# Revit family: LAMP_FIL 35 CORNER OPAL COMFORT TRIMLESS HC
name_source: partatom
category: Luminarias
revit_build: Autodesk Revit 2018 (Build: 20190510_1515(x64)
units: mm (PartAtom-declared; Revit-internal decimal feet)

## family parameters
Anfitrión = Cara
Compartido = No
Corte con vacíos al cargar = No
Cota de conector redondo = Diámetro de uso
Origen de luz = Sí
Punto de cálculo de habitación = No
Tipo de pieza = Normal

## types (4) — shared parameters
Archivo de red fotométrica = F31SF084LOOP830NB.IES
CRI = 80
Cambio de temperatura de color de luz atenuada = <Ninguno>
Dimensions = 311x311x35
Elevación por defecto = 1219 mm
Fabricante = LAMP
Filtro de color = 16777215
Finish = Matte white RAL 9010
Gear = Electronic
IEE = A+
Installation instructions = https://www.lamp.es
Insulation class = I
LED Lifetime = 60.000 L80 B10
Lamp = MID-POWER LED
Last update = 24/05/2021
MacAdam = 3
Manufacturer URL = http://www.lamp.es
Manufacturer country = Spain
Manufacturer name = LAMP
Material difusor = LAMP_PC Difusor Opal Fil
Material suspension = LAMP_Acero genérico
Plum = 6 W
Power = 5 W
Power Supply = 220-240V 50/60Hz
Product URL = https://www.lamp.es
Product datasheet = http://www.lamp.es
Protection rating = IP20 / IK07
Recessed dimensions = 317x317x52
Type = MID POWER TRIDONIC
Weight = 1.23 kg
Ángulo de inclinación = -90.00°

## per-type parameters (varying)
| type | Descripción | Efficacy | Material perfil | Modelo | Product code | Second light |
| 534LM 3000K DALI WHITE | FIL35 HOR CORNER TRIM 800 WW OP DA COM W | 88 lm/W | LAMP_Aluminio Perfil Fil NG | F31TRHCLOOC830DW | F31TRHCLOOC830DW | LAMP_FIL 35 CORNER OPAL COMFORT SURFACE_SECOND : 3000K |
| 534LM 4000K DALI WHITE | FIL35 HOR CORNER TRIM 800 NW OP DA COM W | 88 lm/W | LAMP_Aluminio Perfil Fil GR | F31TRHCLOOC840DW | F31TRHCLOOC840DW | LAMP_FIL 35 CORNER OPAL COMFORT SURFACE_SECOND : 4000K |
| 534LM 3000K  WHITE | FIL35 HORIZ CORNER TRIM 800 NW OP COM WH | 88 lm/W | LAMP_Aluminio Perfil Fil BL | F31TRHCLOOC840NW | F31TRHCLOOC840NW | LAMP_FIL 35 CORNER OPAL COMFORT SURFACE_SECOND : 3000K |
| 577LM 4000K  WHITE | FIL35 HORIZ CORNER TRIM 800 WW OP COM WH | 95 lm/W | LAMP_Aluminio Perfil Fil NG | F31TRHCLOOC830NW | F31TRHCLOOC830NW | LAMP_FIL 35 CORNER OPAL COMFORT SURFACE_SECOND : 4000K |
